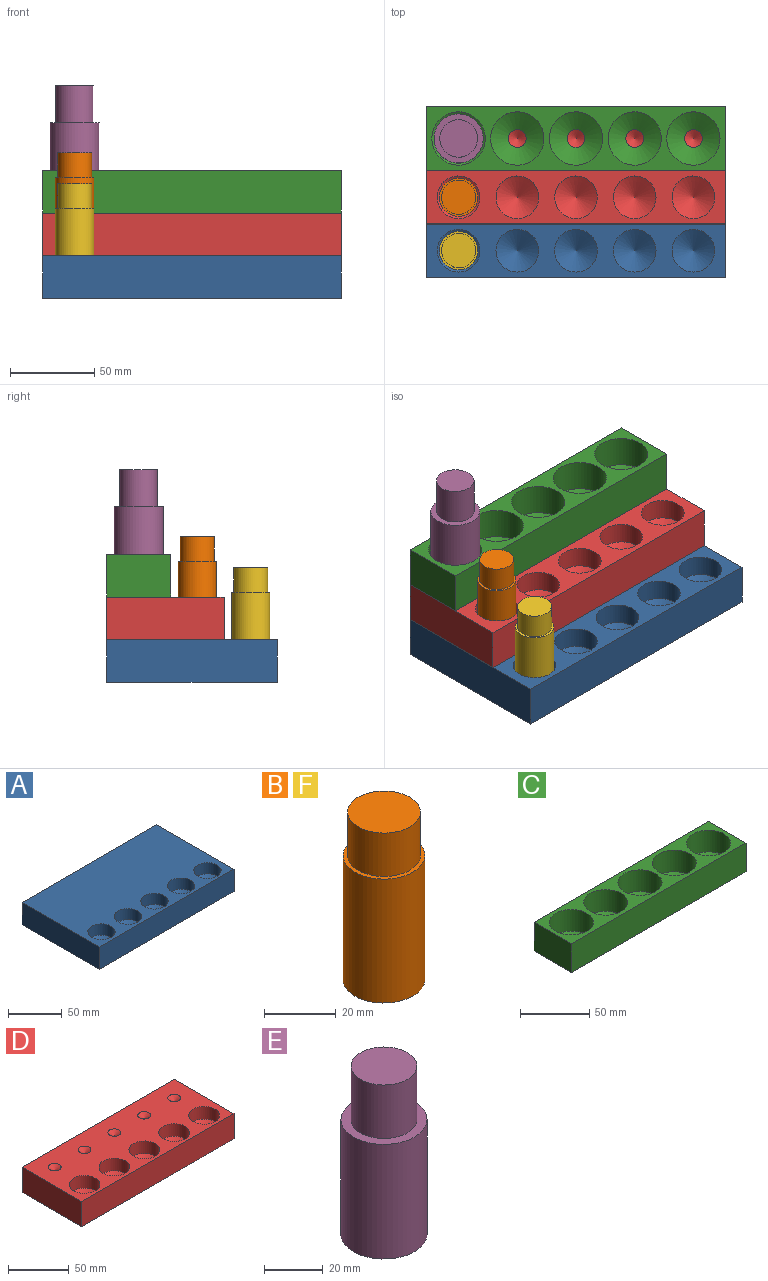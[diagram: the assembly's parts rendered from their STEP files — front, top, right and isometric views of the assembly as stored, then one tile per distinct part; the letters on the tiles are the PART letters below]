
ASSEMBLY  parts=6 mates=5
PART A: 16 faces, bbox 177.8x101.6x25.4 mm
  f0: plane 177.8x101.6mm, normal (0,0,1), area 15530.9mm2, adj f1,f3,f4,f5,f7,f9,f11,f13
  f1: plane 177.8x25.4mm, normal (0,-1,0), area 4516.1mm2, adj f0,f2,f4,f5
  f2: plane 177.8x101.6mm, normal (0,0,-1), area 18064.5mm2, adj f1,f3,f4,f5
  f3: plane 177.8x25.4mm, normal (0,1,0), area 4516.1mm2, adj f0,f2,f4,f5
  f4: plane 101.6x25.4mm, normal (1,0,0), area 2580.6mm2, adj f0,f1,f2,f3
  f5: plane 101.6x25.4mm, normal (-1,0,0), area 2580.6mm2, adj f0,f1,f2,f3
  f6: cone r=0mm half-angle=59deg, axis (0,0,1), area 591.1mm2, adj f7
  f7: cylinder r=12.7mm len=25.4mm, axis (0,0,1), area 1013.4mm2, adj f0,f6
  f8: cone r=0mm half-angle=59deg, axis (0,0,1), area 591.1mm2, adj f9
  f9: cylinder r=12.7mm len=25.4mm, axis (0,0,1), area 1013.4mm2, adj f0,f8
  f10: cone r=0mm half-angle=59deg, axis (0,0,1), area 591.1mm2, adj f11
  f11: cylinder r=12.7mm len=25.4mm, axis (0,0,1), area 1013.4mm2, adj f0,f10
  f12: cone r=0mm half-angle=59deg, axis (0,0,1), area 591.1mm2, adj f13
  f13: cylinder r=12.7mm len=25.4mm, axis (0,0,1), area 1013.4mm2, adj f0,f12
  f14: cone r=0mm half-angle=59deg, axis (0,0,1), area 591.1mm2, adj f15
  f15: cylinder r=12.7mm len=25.4mm, axis (0,0,1), area 1013.4mm2, adj f0,f14
PART B: 5 faces, bbox 22.9x22.9x57.2 mm
  f0: plane 22.86x22.86mm, normal (0,0,-1), area 410.4mm2, adj f1
  f1: cylinder r=11.43mm len=42.32mm, axis (0,0,-1), area 3039.5mm2, adj f0,f2
  f2: plane 22.86x22.86mm, normal (0,0,1), area 86.1mm2, adj f1,f3
  f3: cylinder r=10.16mm len=20.32mm, axis (0,0,-1), area 946.5mm2, adj f2,f4
  f4: plane 20.32x20.32mm, normal (0,0,1), area 324.3mm2, adj f3
PART C: 16 faces, bbox 177.8x38.1x25.4 mm
  f0: plane 38.1x25.4mm, normal (1,0,0), area 967.7mm2, adj f1,f3,f4,f5
  f1: plane 177.8x38.1mm, normal (0,0,1), area 2815.5mm2, adj f0,f2,f3,f4,f7,f9,f11,f13
  f2: plane 38.1x25.4mm, normal (-1,0,0), area 967.7mm2, adj f1,f3,f4,f5
  f3: plane 177.8x25.4mm, normal (0,-1,0), area 4516.1mm2, adj f0,f1,f2,f5
  f4: plane 177.8x25.4mm, normal (0,1,0), area 4516.1mm2, adj f0,f1,f2,f5
  f5: plane 177.8x38.1mm, normal (0,0,-1), area 6331.8mm2, adj f0,f2,f3,f4,f6,f8,f10,f12
  f6: cone r=0mm half-angle=59deg, axis (0,0,1), area 820.4mm2, adj f5,f7
  f7: cylinder r=15.88mm len=31.75mm, axis (0,0,1), area 1900.2mm2, adj f1,f6
  f8: cone r=0mm half-angle=59deg, axis (0,0,1), area 820.4mm2, adj f5,f9
  f9: cylinder r=15.88mm len=31.75mm, axis (0,0,1), area 1900.2mm2, adj f1,f8
  f10: cone r=0mm half-angle=59deg, axis (0,0,1), area 820.4mm2, adj f5,f11
  f11: cylinder r=15.88mm len=31.75mm, axis (0,0,1), area 1900.2mm2, adj f1,f10
  f12: cone r=0mm half-angle=59deg, axis (0,0,1), area 820.4mm2, adj f5,f13
  f13: cylinder r=15.88mm len=31.75mm, axis (0,0,1), area 1900.2mm2, adj f1,f12
  f14: cone r=0mm half-angle=59deg, axis (0,0,1), area 820.4mm2, adj f5,f15
  f15: cylinder r=15.88mm len=31.75mm, axis (0,0,1), area 1900.2mm2, adj f1,f14
PART D: 21 faces, bbox 177.8x69.9x25.4 mm
  f0: plane 69.85x25.4mm, normal (1,0,0), area 1774.2mm2, adj f1,f3,f4,f5
  f1: plane 177.8x25.4mm, normal (0,-1,0), area 4516.1mm2, adj f0,f2,f3,f4
  f2: plane 69.85x25.4mm, normal (-1,0,0), area 1774.2mm2, adj f1,f3,f4,f5
  f3: plane 177.8x69.85mm, normal (0,0,-1), area 12419.3mm2, adj f0,f1,f2,f5
  f4: plane 177.8x69.85mm, normal (0,0,1), area 9443.4mm2, adj f0,f1,f2,f5,f7,f9,f11,f13
  f5: plane 177.8x25.4mm, normal (0,1,0), area 4516.1mm2, adj f0,f2,f3,f4
  f6: cone r=0mm half-angle=59deg, axis (0,0,1), area 591.1mm2, adj f7
  f7: cylinder r=12.7mm len=25.4mm, axis (0,0,1), area 1013.4mm2, adj f4,f6
  f8: cone r=0mm half-angle=59deg, axis (0,0,1), area 591.1mm2, adj f9
  f9: cylinder r=12.7mm len=25.4mm, axis (0,0,1), area 1013.4mm2, adj f4,f8
  f10: cone r=0mm half-angle=59deg, axis (0,0,1), area 591.1mm2, adj f11
  f11: cylinder r=12.7mm len=25.4mm, axis (0,0,1), area 1013.4mm2, adj f4,f10
  f12: cone r=0mm half-angle=59deg, axis (0,0,1), area 591.1mm2, adj f13
  f13: cylinder r=12.7mm len=25.4mm, axis (0,0,1), area 1013.4mm2, adj f4,f12
  f14: cone r=0mm half-angle=59deg, axis (0,0,1), area 591.1mm2, adj f15
  f15: cylinder r=12.7mm len=25.4mm, axis (0,0,1), area 1013.4mm2, adj f4,f14
  f16: cone r=0mm half-angle=59deg, axis (0,0,1), area 103.2mm2, adj f4
  f17: cone r=0mm half-angle=59deg, axis (0,0,1), area 103.2mm2, adj f4
  f18: cone r=0mm half-angle=59deg, axis (0,0,1), area 103.2mm2, adj f4
  f19: cone r=0mm half-angle=59deg, axis (0,0,1), area 103.2mm2, adj f4
  f20: cone r=0mm half-angle=59deg, axis (0,0,1), area 103.2mm2, adj f4
PART E: 5 faces, bbox 29.2x29.2x69.9 mm
  f0: plane 29.21x29.21mm, normal (0,0,-1), area 670.1mm2, adj f4
  f1: plane 22.35x22.35mm, normal (0,0,1), area 392.4mm2, adj f2
  f2: cylinder r=11.18mm len=22.35mm, axis (0,0,-1), area 1560.7mm2, adj f1,f3
  f3: plane 29.21x29.21mm, normal (0,0,1), area 277.7mm2, adj f2,f4
  f4: cylinder r=14.61mm len=47.63mm, axis (0,0,-1), area 4370.4mm2, adj f0,f3
PART F: same geometry as B
PLACE A at identity
PLACE B t=(-9.16,47.62,29.64)mm
PLACE C at identity
PLACE D at identity
PLACE E t=(58.12,82.55,56.8)mm
PLACE F t=(-9.16,15.87,11.21)mm
MATE fastened D.f2 <-> A.f5  axis (-1,0,0) through (0,101.6,25.4)mm
MATE fastened C.f2 <-> D.f2  axis (-1,0,0) through (0,101.6,50.8)mm
MATE slider F.f1 <-> A.f6  axis (0,0,-1) through (19.05,15.87,32.37)mm
MATE slider B.f1 <-> D.f14  axis (0,0,-1) through (19.05,47.62,50.8)mm
MATE slider E.f2 <-> C.f14  axis (0,0,-1) through (19.05,82.55,80.61)mm
